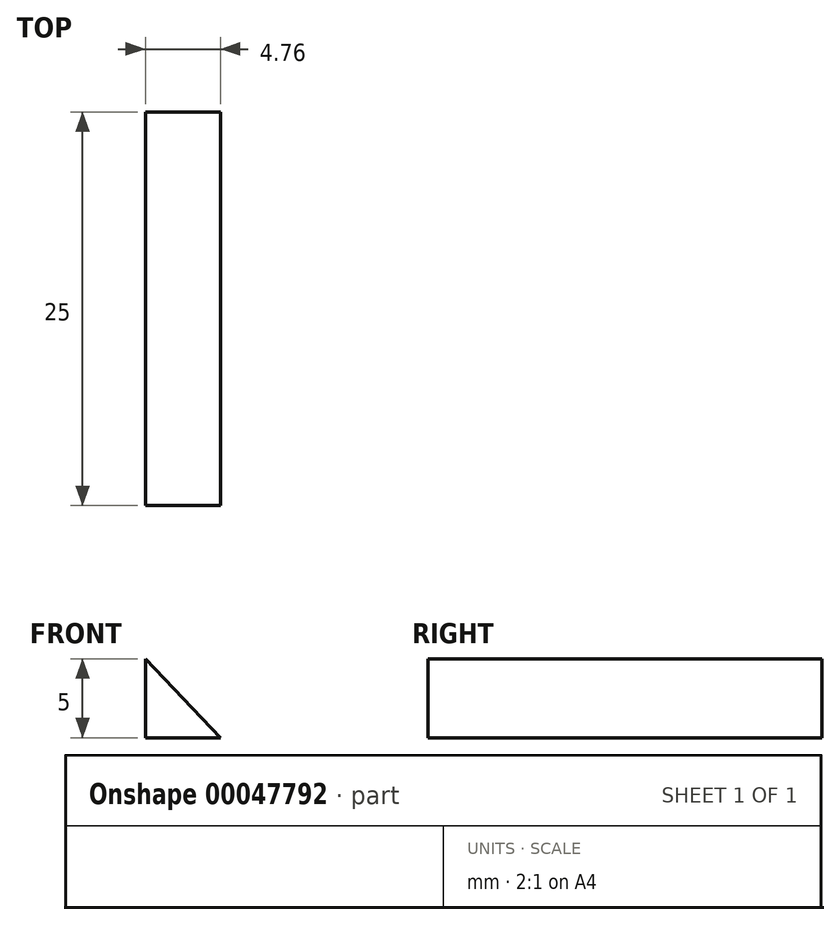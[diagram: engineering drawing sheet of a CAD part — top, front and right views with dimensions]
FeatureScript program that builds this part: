
annotation { "Feature Type Name" : "Feature", "Feature Type Description" : "" }
export const myFeature = defineFeature(function(context is Context, id is Id, definition is map)
    precondition{}
    {
        {
            var Q0;
            Q0=qCreatedBy(makeId("Front.planeOp"),FACE);
            var sketch = newSketch(context, id + "F0", { "sketchPlane" : qUnion([Q0])});
            skLineSegment(sketch, "E0", {"start": v(0, 0) * mm, "end": v(-4.76, 5) * mm});
            skLineSegment(sketch, "E1", {"start": v(-4.76, 5) * mm, "end": v(-4.76, 0) * mm});
            skLineSegment(sketch, "E2", {"start": v(-4.76, 0) * mm, "end": v(0, 0) * mm});
            skSolve(sketch);
        }
        {
            var Q0;
            Q0=makeQuery(id+"F0.imprint","IMPRINT",FACE,{"disambiguationData":[TD([[makeQuery(id+"F0.imprint","IMPRINT",EDGE,{"derivedFrom":sQuery(id+"F0.wireOp",EDGE,"E0")}),1.0]])]});
            extrude(context, id + "F1", {"entities" : qUnion([Q0]), "depth" : 25 * mm});
        }
    });
